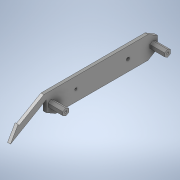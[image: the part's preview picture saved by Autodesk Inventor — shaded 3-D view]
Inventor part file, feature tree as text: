
AUTODESK INVENTOR PART (.ipt)
format: ipt  version: 2020 (Build 240168000, 168)  size: 165,376 bytes
history: native  units: in
note: dims shown in document units (in); Inventor stores cm internally (conversion verified against a paired STEP export)
features: other x3, extrude x1, sketch x1
ambient origin geometry x8: Origin, YZ Plane, XZ Plane, XY Plane, X Axis, Y Axis, Z Axis, Center Point
bodies: Solid1 (feature_tree)
feature tree (5):
  other  "HexWheelGuard.ipt"
  extrude  "Extrusion1"  Depth=0.315in
  other  "Solid1::HexWheelGuard.ipt"
  other  "TaggingFeature1"
  sketch  "Sketch1"  dims[d0=0.3937in d1=0.0787in d4=60.0deg d5=0.315in d6=0.0in d7=0.0in d8=1.3858in]
